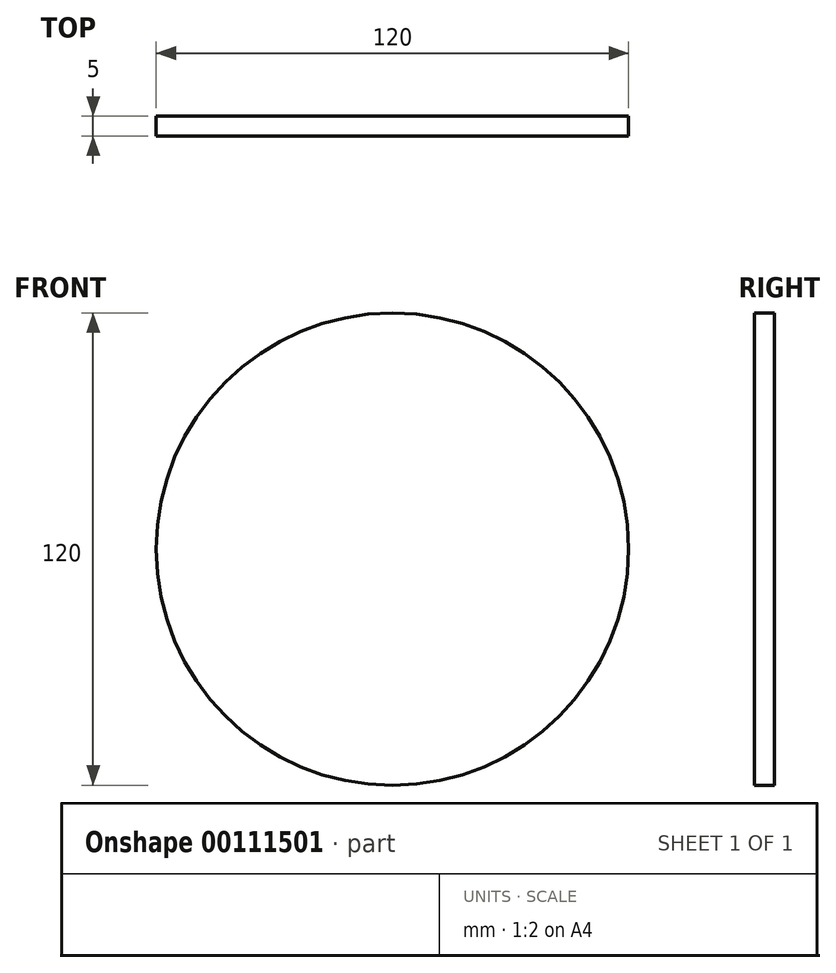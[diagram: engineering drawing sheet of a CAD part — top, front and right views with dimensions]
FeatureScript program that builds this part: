
annotation { "Feature Type Name" : "Feature", "Feature Type Description" : "" }
export const myFeature = defineFeature(function(context is Context, id is Id, definition is map)
    precondition{}
    {
        {
            var Q0;
            Q0=qCreatedBy(makeId("Front.planeOp"),FACE);
            var sketch = newSketch(context, id + "F0", { "sketchPlane" : qUnion([Q0])});
            skCircle(sketch, "E0", {"center": v(0, 0) * mm, "radius": 60 * mm});
            skSolve(sketch);
        }
        {
            var Q0;
            Q0 = qSketchRegion(id + "F0", true);
            extrude(context, id + "F1", {"entities" : qUnion([Q0]), "depth" : 5 * mm});
        }
    });
